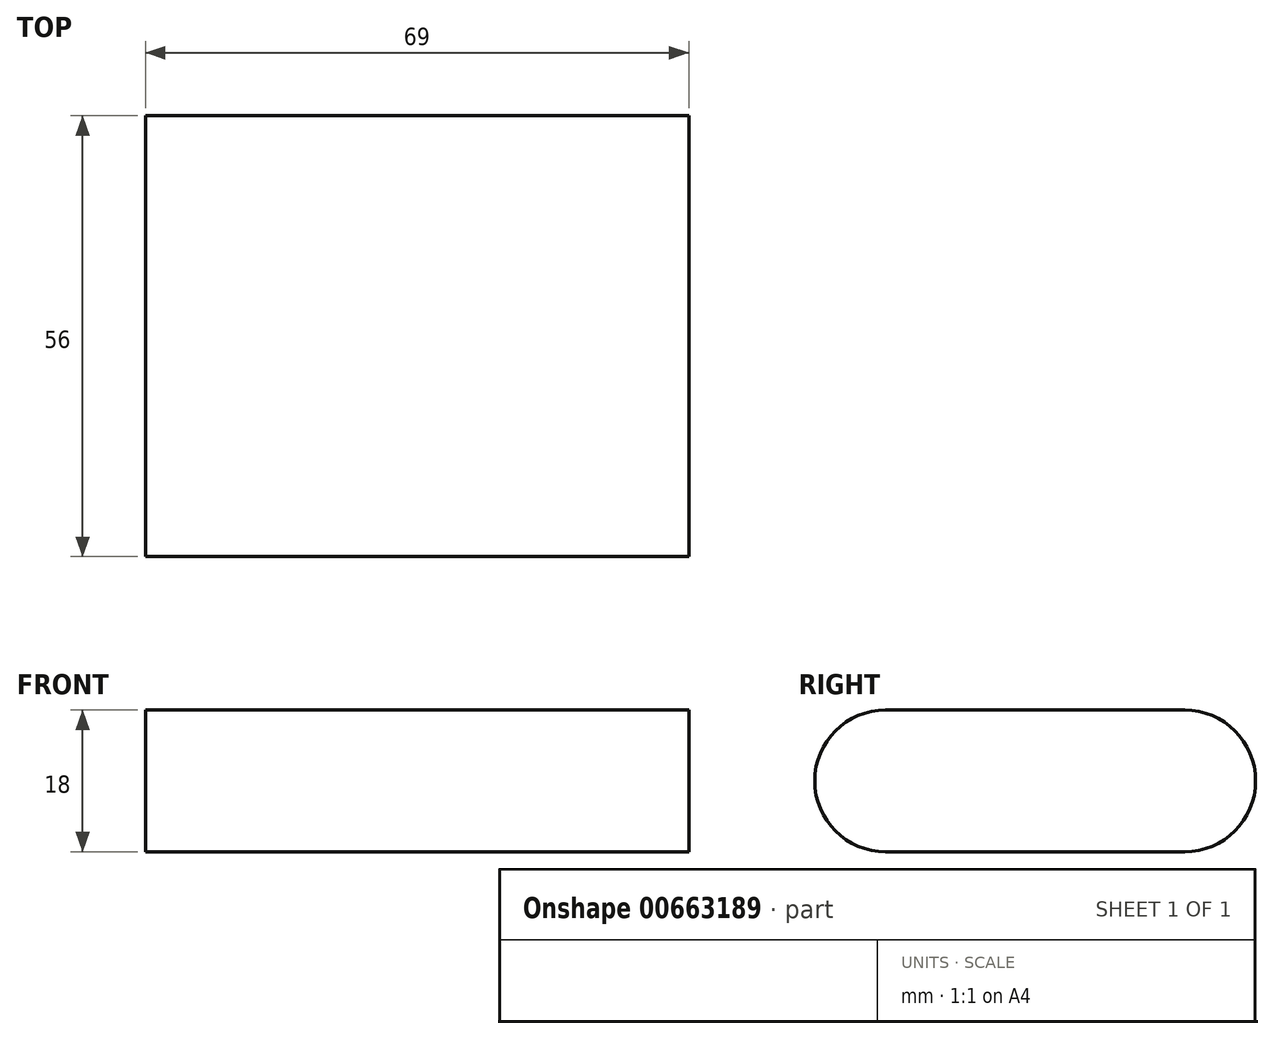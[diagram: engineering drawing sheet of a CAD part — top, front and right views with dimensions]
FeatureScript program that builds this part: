
annotation { "Feature Type Name" : "Feature", "Feature Type Description" : "" }
export const myFeature = defineFeature(function(context is Context, id is Id, definition is map)
    precondition{}
    {
        {
            var Q0;
            Q0=qCreatedBy(makeId("Right.planeOp"),FACE);
            var sketch = newSketch(context, id + "F0", { "sketchPlane" : qUnion([Q0])});
            skLineSegment(sketch, "E0", {"start": v(-19, 0) * mm, "end": v(19, 0) * mm, "construction": true});
            skArc(sketch, "E1.0.startCap", {"start": v(-19, -9) * mm, "mid": v(-28, 0) * mm, "end": v(-19, 9) * mm});
            skArc(sketch, "E1.0.endCap", {"start": v(19, 9) * mm, "mid": v(28, 0) * mm, "end": v(19, -9) * mm});
            skLineSegment(sketch, "E1.0.left", {"start": v(-19, 9) * mm, "end": v(19, 9) * mm});
            skLineSegment(sketch, "E1.0.right", {"start": v(-19, -9) * mm, "end": v(19, -9) * mm});
            skSolve(sketch);
        }
        {
            var Q0;
            Q0 = qSketchRegion(id + "F0", true);
            extrude(context, id + "F1", {"entities" : qUnion([Q0]), "depth" : 69 * mm, "offsetDistance" : 25 * mm});
        }
    });
